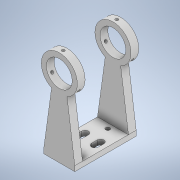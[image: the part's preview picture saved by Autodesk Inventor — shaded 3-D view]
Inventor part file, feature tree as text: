
AUTODESK INVENTOR PART (.ipt)
format: ipt  version: 2021 (Build 250183000, 183)  size: 284,672 bytes
history: native  units: in
note: dims shown in document units (in); Inventor stores cm internally (conversion verified against a paired STEP export)
features: sketch x6, extrude x5, plane x2, pattern_circular x1, mirror x1, hole x1
ambient origin geometry x8: Origin, YZ Plane, XZ Plane, XY Plane, X Axis, Y Axis, Z Axis, Center Point
bodies: Solid1 (feature_tree)
feature tree (16):
  extrude  "Extrusion1"  Depth=0.75in
  extrude  "Extrusion2"  Depth=2.979in TaperAngle=0.0deg
  plane  "Work Plane1"
  extrude  "Extrusion4"  Depth=0.325in
  plane  "Work Plane2"
  extrude  "Extrusion5"  Depth=0.75in
  pattern_circular  "Circular Pattern1"  [2 undecoded]
  mirror  "Mirror1"
  extrude  "Extrusion7"  Depth=0.625in
  hole  "Hole1"  [1 undecoded]
  sketch  "Sketch1"  dims[d0=6.0in d1=0.75in]
  sketch  "Sketch2"  dims[d2=0.5in d3=2.979in d4=0.0in]
  sketch  "Sketch5"  dims[d5=0.375in d6=0.325in]
  sketch  "Sketch6"  dims[d7=0.6in d8=0.75in]
  sketch  "Sketch20"  dims[d9=0.0in d10=0.0in]
  sketch  "Sketch22"  dims[d15=1.25in d16=0.25in d17=4.0in d18=0.375in d19=0.375in d20=0.0in d21=0.1875in d22=0.136in d23=0.0in d24=0.0in d25=1.1811in d26=360.0deg d51=0.0039in d53=60.0deg d72=0.0039in d74=60.0deg d93=0.0039in d95=60.0deg d114=0.0039in d116=60.0deg d135=0.0039in d137=60.0deg d156=0.0039in d158=60.0deg d168=0.125in d169=0.0in d170=0.325in d173=0.25in d174=0.25in d175=0.201in d176=0.38in d177=0.375in d178=0.125in d179=0.5635in d180=1.0in d181=0.8108in d183=0.625in]
note: 3 required parameter values undecoded (feature->parameter linkage not recoverable at this tier; creation-order binding heuristic only, values carry confidence <= 0.55)
